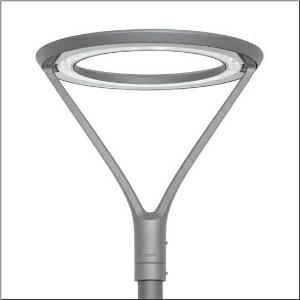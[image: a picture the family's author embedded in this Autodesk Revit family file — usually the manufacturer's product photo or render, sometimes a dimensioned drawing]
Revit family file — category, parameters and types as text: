
# Revit family: dl_r__20___pl1_2s_5xa51283ws008_843d
name_source: partatom
category: Lighting Fixtures
units: mm (PartAtom-declared; Revit-internal decimal feet)

## family parameters
Cut with Voids When Loaded = No
Host = Face
Light Source = No
Part Type = Normal
Room Calculation Point = No
Round Connector Dimension = Use Diameter
Shared = No

## types (1)
- --- (1 x LED, 3080 lm, 24.6 W, 3000K)
    Apparent Load = 25 VA
    CIE Flux Codes = 33 78 99 100 100
    Color Rendering = 70
    Color Temperature = 3000K
    Default Elevation = 1800 mm
    Description = DL® 20, mast luminaire, primary light control with reflector, highly specular, primary optical cover: cover, of toughened safety glass of clear glass with excellent transmission level, light distribution: PL1.2s, light emission: direct distribution, primary light characteristic: symmetric, installation type: post-top, LED, High Power LED, rated luminous flux: 3.040lm, luminous efficacy: 86lm/W, light colour: 730, colour temperature: 3000K, control gear: Plus, control: overheat protection, power reduction, digital communication interface, constant luminous flux control, time-dependent luminous flux control, flexible luminous flux parameterisation, electronic power reduction, mains connection: 230..240V, 50/60Hz, connection cable pre-assembled, cable length: 5m, start of lifetime: 36W, end of service life: 36W, reduction: 17W, luminaire housing, upper part, of cast aluminium, powder-coated, Siteco® metallic grey (DB 702S), diameter: 690mm, height: 690mm, spigot size: 76mm (post-top), mounting height: 4..6m, luminaire housing, of cast aluminium, powder-coated, Siteco® metallic grey (DB 702S), equipment: standard, protection rating (complete): IP66, insulation class (complete): insulation class II (safety insulation), certification: CE, ENEC, VDE, impact resistance: IK08, permissible operating ambient temperature: -25..+35°C, standard-compliant lighting for roads and squares, packaging unit: 1 piece

Light Distribution: PL1.2s
    Height = 690 mm
    Lamp = 1 x LED
    Lamp Light Flux = 3080 lm
    Lamp Power = 24.6 W
    Lamp count = 1
    Length = 690 mm
    Luminous efficacy = 125 lm/W
    Manufacturer = Siteco
    ModVariant = No
    Model = 5XA51283WS008
    Number of Poles = 1
    OnlyDefault = Yes
    Power Factor = 1
    Product Name = DL® 20 | PL1.2s
    Product group = mast luminaire | pylon top
    ProductGroupID = 6100
    Protection Class = Protection class II
    Protection Degree = IP 66
    RLX_Detail_Level = 1
    RLX_Emergency_Light_Flux = 0 lm
    RLX_Emergency_Type = 0
    RLX_Emergency_Type_DB = No
    RlxData = <blob elided: 204437 chars, md5=87c6f732>
    Socket = socket
    Standby Power = 0 W
    System Light Flux = 3080 lm
    System Power = 25 W
    Type Comments = factory setting: luminous flux: 100 % | dim-lin: 254 | 330 mA
    Type Image = l_1006001.jpg
    URL = http://relux.com
    VarID = @adj_076940
    Voltage = 0 V
    Weight = 0.00 kg
    Width = 0 mm  [stored 0 ft]

note: [stored X ft] marks values corroborated as IEEE doubles in the binary element streams (Revit-internal decimal feet)

## geometry (parser evidence)
native form markers: Blend x4, Sweep x10
no freeform markers — native parametric forms only
